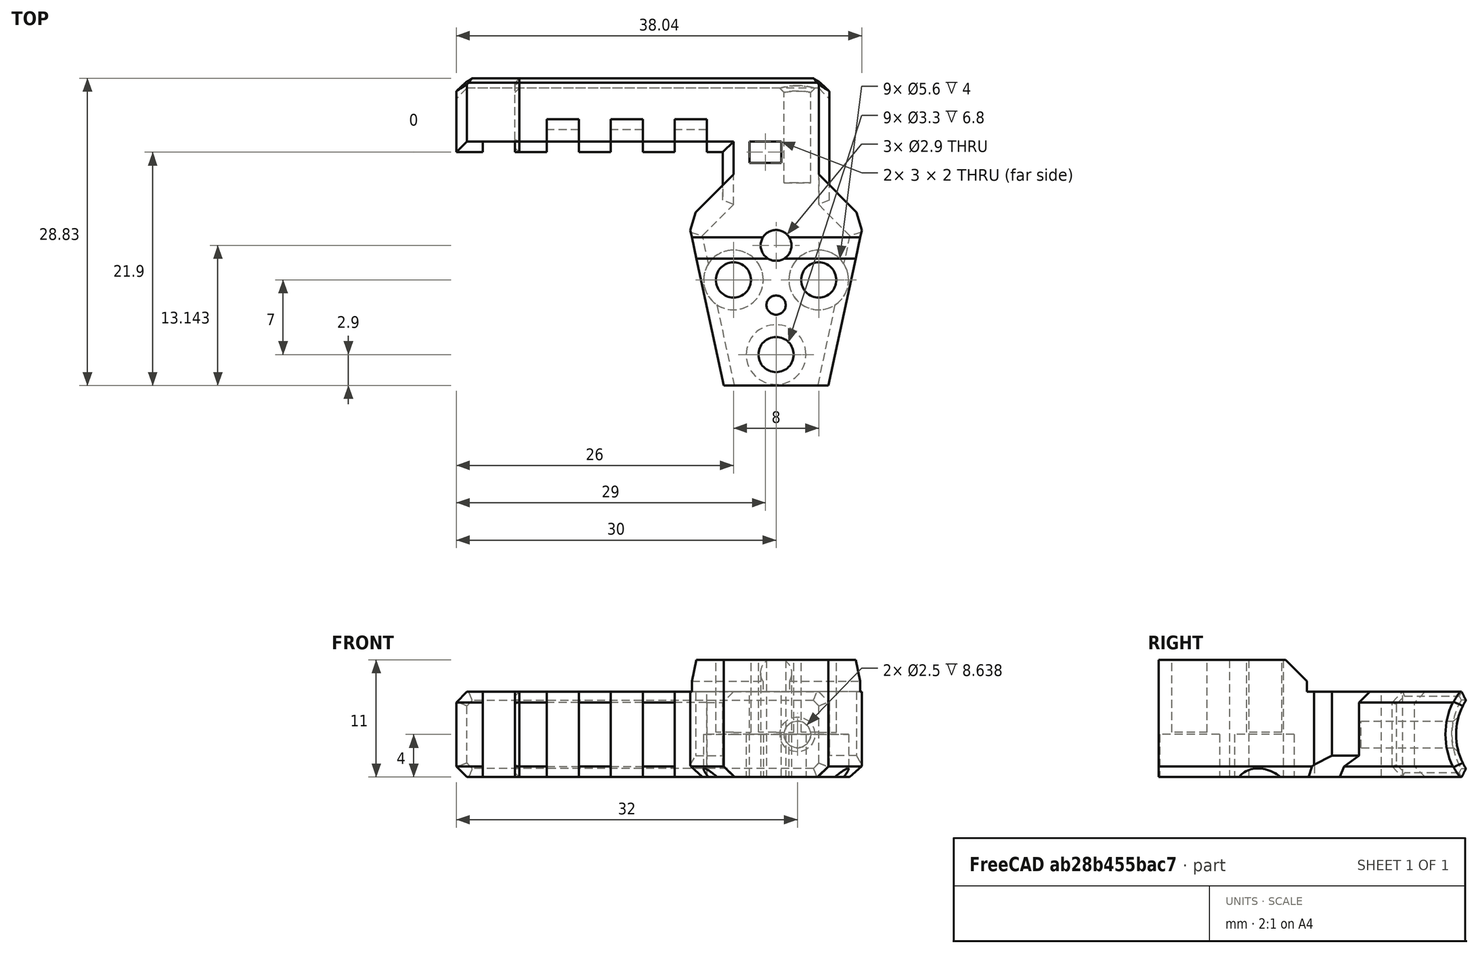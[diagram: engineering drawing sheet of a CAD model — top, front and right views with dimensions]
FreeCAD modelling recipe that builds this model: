
FCSTD DOCUMENT  (FreeCAD 0.19R24291 (Git))
Label: cable-mounter
License: Other
LicenseURL: GPL3
objects: Part::Box×10, Part::Cut×5, Part::Chamfer×5, Part::Feature×4, Part::MultiFuse×4, Part::Cylinder×2
note: 30 computed .brp shape members not serialized (recipe doc carries the construction recipe); baked Part::Feature solids carry a one-line shape summary decoded from their .brp

FEATURE [Part::Feature] Part__Feature027  label="unversal_cable_mount"
  Placement = pos=(0,-0.1,8) rot=(-1,0,0;1.5708rad)
  shape: bbox 16.08 x 48.8 x 11 mm, 57 faces (baked)
FEATURE [Part::Box] Box  label="Cube"
  AttacherType = Attacher::AttachEngine3D
  Height = 10
  Length = 12
  Placement = pos=(-6,22.9,0) rot=(0,0,1;0rad)
  Width = 36
FEATURE [Part::Box] Box001  label="Cube001"
  AttacherType = Attacher::AttachEngine3D
  Height = 8
  Length = 35
  Placement = pos=(-30,21.9,0) rot=(0,0,1;0rad)
  Width = 8
FEATURE [Part::Cut] Cut
  Base = -> Part__Feature027
  Tool = -> Box
FEATURE [Part::Cylinder] Cylinder
  Angle = 360
  AttacherType = Attacher::AttachEngine3D
  Height = 47
  Placement = pos=(10,33.9,4) rot=(0,-1,0;1.5708rad)
  Radius = 6
FEATURE [Part::Box] Box002  label="Cube002"
  AttacherType = Attacher::AttachEngine3D
  Height = 10
  Length = 3
  Placement = pos=(-2.5,20.9,0) rot=(0,0,1;0rad)
  Width = 2
FEATURE [Part::Box] Box003  label="Cube003"
  AttacherType = Attacher::AttachEngine3D
  Height = 10
  Length = 3
  Placement = pos=(-27.5,20.9,0) rot=(0,0,1;0rad)
  Width = 2
FEATURE [Part::Box] Box004  label="Cube004"
  AttacherType = Attacher::AttachEngine3D
  Height = 10
  Length = 3
  Placement = pos=(-21.5,20.9,0) rot=(0,0,1;0rad)
  Width = 2
FEATURE [Part::Box] Box005  label="Cube005"
  AttacherType = Attacher::AttachEngine3D
  Height = 10
  Length = 3
  Placement = pos=(-15.5,20.9,0) rot=(0,0,1;0rad)
  Width = 2
FEATURE [Part::Box] Box006  label="Cube006"
  AttacherType = Attacher::AttachEngine3D
  Height = 10
  Length = 3
  Placement = pos=(-9.5,20.9,0) rot=(0,0,1;0rad)
  Width = 2
FEATURE [Part::MultiFuse] Fusion
  Shapes = -> [Box006,Box005,Box004,Box003]
FEATURE [Part::MultiFuse] Fusion002
  Shapes = -> [Fusion,Box002]
FEATURE [Part::Chamfer] Chamfer
  Base = -> Box001
  Edges = 6 edges r=1: [Edge2,Edge4,Edge6,Edge8,Edge9,Edge10]
FEATURE [Part::MultiFuse] Fusion003
  Shapes = -> [Chamfer,Cut]
FEATURE [Part::Cut] Cut001
  Base = -> Fusion003
  Tool = -> Fusion002
FEATURE [Part::Cut] Cut002
  Base = -> Cut001
  Tool = -> Cylinder
FEATURE [Part::Chamfer] Chamfer001
  Base = -> Cut002
  Edges = 8 edges r=1: [Edge3,Edge10,Edge11,Edge12,Edge13,Edge14,Edge15,Edge16]
FEATURE [Part::Feature] Chamfer001001  label="cable-mounter"
  shape: bbox 38.38 x 29.43 x 11.83 mm, 81 faces (baked)
FEATURE [Part::Cylinder] Cylinder001
  Angle = 360
  AttacherType = Attacher::AttachEngine3D
  Height = 10
  Placement = pos=(2,19,4) rot=(0.57735,-0.57735,-0.57735;4.18879rad)
  Radius = 1.25
FEATURE [Part::Cut] Cut003
  Base = -> Chamfer001001
  Tool = -> Cylinder001
FEATURE [Part::Chamfer] Chamfer001002
  Base = -> Cut003
  Edges = 1 edges r=0.4: [Edge207]
FEATURE [Part::Feature] Cut004001001
  shape: bbox 32.54 x 29.43 x 11.83 mm, 73 faces (baked)
FEATURE [Part::Chamfer] Chamfer001003
  Base = -> Cut004001001
  Edges = 8 edges r=0.4: [Edge1,Edge10,Edge22,Edge44,Edge50,Edge85,Edge89,Edge91]
FEATURE [Part::Box] Box007  label="Cube007"
  AttacherType = Attacher::AttachEngine3D
  Height = 10
  Length = 3
  Placement = pos=(-21.5,21,0) rot=(0,0,1;0rad)
  Width = 3
FEATURE [Part::Box] Box008  label="Cube008"
  AttacherType = Attacher::AttachEngine3D
  Height = 10
  Length = 3
  Placement = pos=(-15.5,21,0) rot=(0,0,1;0rad)
  Width = 3
FEATURE [Part::Box] Box009  label="Cube009"
  AttacherType = Attacher::AttachEngine3D
  Height = 10
  Length = 3
  Placement = pos=(-9.5,21,0) rot=(0,0,1;0rad)
  Width = 3
FEATURE [Part::MultiFuse] Fusion004
  Shapes = -> [Box009,Box008,Box007]
FEATURE [Part::Cut] Cut004001002
  Base = -> Chamfer001003
  Tool = -> Fusion004
FEATURE [Part::Chamfer] Chamfer001004
  Base = -> Cut004001002
  Edges = 6 edges r=1: [Edge43,Edge47,Edge51,Edge70,Edge74,Edge78]
FEATURE [Part::Feature] Chamfer001004001
  shape: bbox 32.54 x 29.43 x 11.83 mm, 93 faces (baked)
